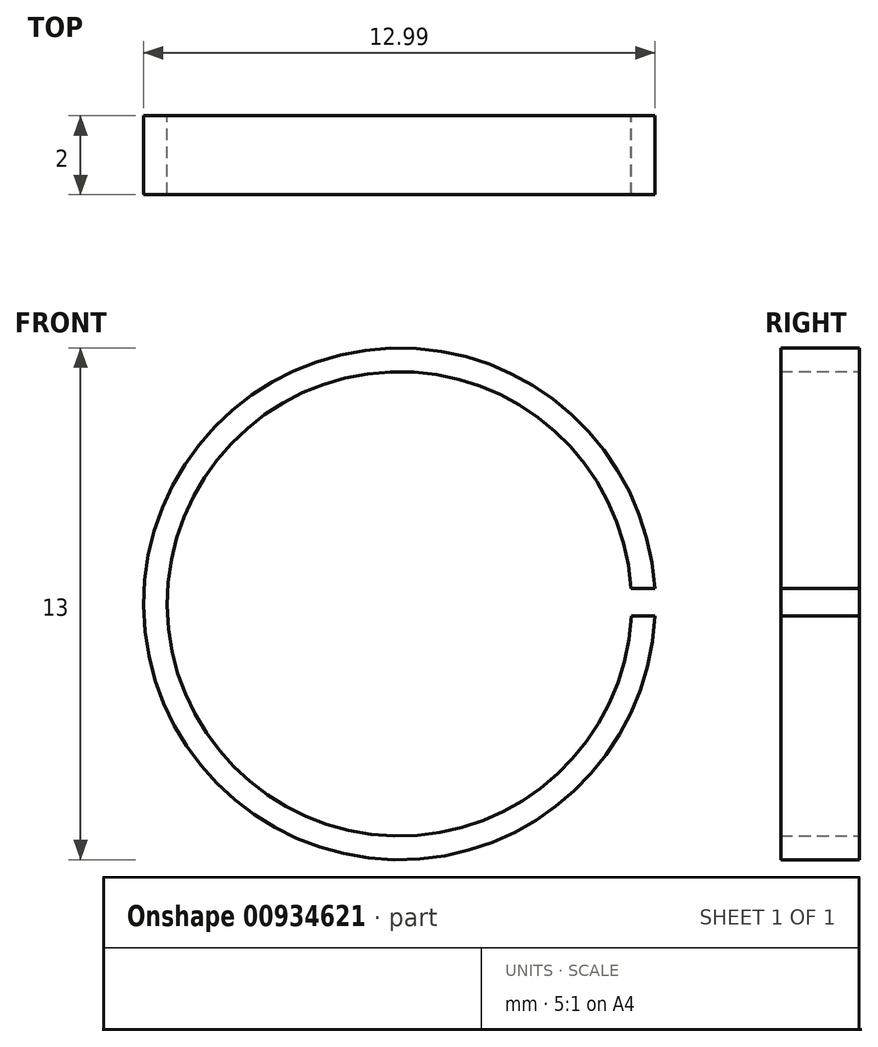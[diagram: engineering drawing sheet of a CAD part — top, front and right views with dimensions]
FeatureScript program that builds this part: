
annotation { "Feature Type Name" : "Feature", "Feature Type Description" : "" }
export const myFeature = defineFeature(function(context is Context, id is Id, definition is map)
    precondition{}
    {
        {
            var Q0;
            Q0=qCreatedBy(makeId("Front.planeOp"),FACE);
            var sketch = newSketch(context, id + "F0", { "sketchPlane" : qUnion([Q0])});
            skArc(sketch, "E0", {"start": v(5.89, 0.4) * mm, "mid": v(-5.9, -0.04) * mm, "end": v(5.9, -0.3) * mm});
            skArc(sketch, "E1", {"start": v(6.49, 0.4) * mm, "mid": v(-6.5, -0.04) * mm, "end": v(6.5, -0.3) * mm});
            skLineSegment(sketch, "E2", {"start": v(5.89, 0.4) * mm, "end": v(6.49, 0.4) * mm});
            skLineSegment(sketch, "E3", {"start": v(5.9, -0.3) * mm, "end": v(6.5, -0.3) * mm});
            skSolve(sketch);
        }
        {
            var Q0;
            Q0=makeQuery(id+"F0.imprint","IMPRINT",FACE,{"disambiguationData":[TD([[makeQuery(id+"F0.imprint","IMPRINT",EDGE,{"derivedFrom":sQuery(id+"F0.wireOp",EDGE,"E0")}),-1.0]])]});
            extrude(context, id + "F1", {"entities" : qUnion([Q0]), "depth" : 2 * mm, "offsetDistance" : 25 * mm});
        }
    });
